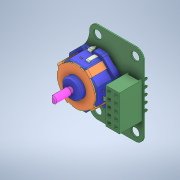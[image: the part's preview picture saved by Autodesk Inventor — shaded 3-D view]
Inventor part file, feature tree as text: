
AUTODESK INVENTOR PART (.ipt)
format: ipt  version: 2020 (Build 240168000, 168)  size: 7,990,784 bytes
history: native  units: mm
features: imported_body x45, other x4, extrude x1, sketch x1
ambient origin geometry x8: Origin, YZ Plane, XZ Plane, XY Plane, X Axis, Y Axis, Z Axis, Center Point
bodies: Volumenkörper1 (feature_tree), Volumenkörper2 (feature_tree), Volumenkörper3 (feature_tree), Volumenkörper4 (feature_tree), Volumenkörper5 (feature_tree), Volumenkörper6 (feature_tree), Volumenkörper7 (feature_tree), Volumenkörper8 (feature_tree), Volumenkörper9 (feature_tree), Volumenkörper10 (feature_tree), Volumenkörper11 (feature_tree), Volumenkörper12 (feature_tree), Volumenkörper13 (feature_tree), Volumenkörper14 (feature_tree), Volumenkörper15 (feature_tree), Volumenkörper16 (feature_tree), Volumenkörper17 (feature_tree), Volumenkörper18 (feature_tree), Volumenkörper19 (feature_tree), Volumenkörper20 (feature_tree), Volumenkörper21 (feature_tree), Volumenkörper22 (feature_tree), Volumenkörper23 (feature_tree), Volumenkörper24 (feature_tree), Volumenkörper25 (feature_tree), Volumenkörper26 (feature_tree), Volumenkörper27 (feature_tree), Volumenkörper28 (feature_tree), Volumenkörper29 (feature_tree), Volumenkörper30 (feature_tree), Volumenkörper31 (feature_tree), Volumenkörper32 (feature_tree), Volumenkörper33 (feature_tree), Volumenkörper34 (feature_tree), Volumenkörper35 (feature_tree), Volumenkörper36 (feature_tree), Volumenkörper37 (feature_tree), Volumenkörper38 (feature_tree), Volumenkörper39 (feature_tree), Volumenkörper40 (feature_tree), Volumenkörper41 (feature_tree), Volumenkörper42 (feature_tree), Volumenkörper43 (feature_tree), Volumenkörper44 (feature_tree), Volumenkörper45 (feature_tree)
feature tree (51):
  other  "Kombinieren1"
  other  "Formen1"
  extrude  "Extrusion1"  Depth=30.0mm
  sketch  "Skizze1"  dims[d0=40.0mm d1=40.0mm d3=60.0mm d4=30.0mm d5=100.0mm d6=0.0mm]
  imported_body  "Basis1"
  imported_body  "Basis2"
  imported_body  "Basis3"
  imported_body  "Basis4"
  imported_body  "Basis5"
  imported_body  "Basis6"
  imported_body  "Basis7"
  imported_body  "Basis8"
  imported_body  "Basis9"
  imported_body  "Basis10"
  imported_body  "Basis11"
  imported_body  "Basis12"
  imported_body  "Basis13"
  imported_body  "Basis14"
  imported_body  "Basis15"
  imported_body  "Basis16"
  imported_body  "Basis17"
  imported_body  "Basis18"
  imported_body  "Basis19"
  imported_body  "Basis20"
  imported_body  "Basis21"
  imported_body  "Basis22"
  imported_body  "Basis23"
  imported_body  "Basis24"
  imported_body  "Basis25"
  imported_body  "Basis26"
  imported_body  "Basis27"
  imported_body  "Basis28"
  imported_body  "Basis29"
  imported_body  "Basis30"
  imported_body  "Basis31"
  imported_body  "Basis32"
  imported_body  "Basis33"
  imported_body  "Basis34"
  imported_body  "Basis35"
  imported_body  "Basis36"
  imported_body  "Basis37"
  imported_body  "Basis38"
  imported_body  "Basis39"
  imported_body  "Basis40"
  imported_body  "Basis41"
  imported_body  "Basis42"
  imported_body  "Basis43"
  imported_body  "Basis44"
  imported_body  "Basis45"
  other  "Zusammengesetzt1"
  other  "Flä1"
